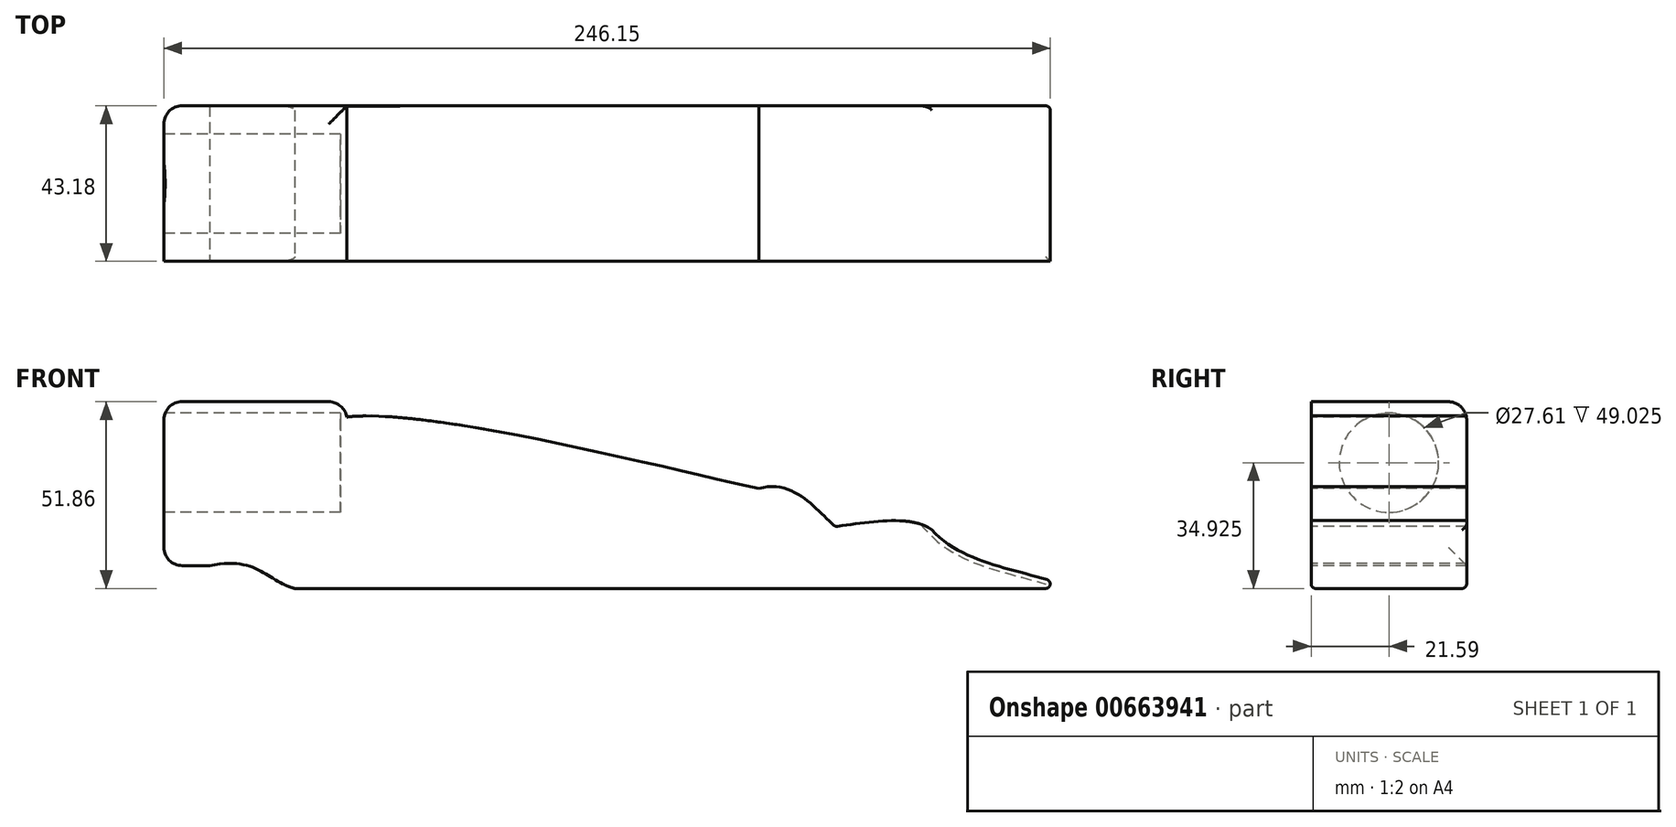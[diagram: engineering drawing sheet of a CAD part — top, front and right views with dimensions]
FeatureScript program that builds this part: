
annotation { "Feature Type Name" : "Feature", "Feature Type Description" : "" }
export const myFeature = defineFeature(function(context is Context, id is Id, definition is map)
    precondition{}
    {
        {
            var Q0;
            Q0=qCreatedBy(makeId("Front.planeOp"),FACE);
            var sketch = newSketch(context, id + "F0", { "sketchPlane" : qUnion([Q0])});
            skLineSegment(sketch, "E0", {"start": v(0, 0) * mm, "end": v(304.8, 0) * mm});
            skLineSegment(sketch, "E1", {"start": v(0, 0) * mm, "end": v(0, 69.85) * mm});
            skLineSegment(sketch, "E2", {"start": v(304.8, 0) * mm, "end": v(304.8, 17.78) * mm});
            skLineSegment(sketch, "E3", {"start": v(304.8, 17.78) * mm, "end": v(0, 69.85) * mm});
            skSolve(sketch);
        }
        {
            var Q0;
            Q0=qSketchRegion(id+"F0",true);
            extrude(context, id + "F1", {"entities" : qUnion([Q0]), "depth" : 43.18 * mm, "offsetDistance" : 25.4 * mm});
        }
        {
            var Q0;
            Q0=makeQuery(id+"F1.opExtrude","SWEPT_FACE",FACE,{"disambiguationData":[OSD([sQuery(id+"F0.wireOp",EDGE,"E1")])]});
            var sketch = newSketch(context, id + "F2", { "sketchPlane" : qUnion([Q0])});
            skCircle(sketch, "E4", {"center": v(21.59, 31.75) * mm, "radius": 9.53 * mm});
            skSolve(sketch);
        }
        {
            var Q0;
            Q0=qSketchRegion(id+"F2",true);
            extrude(context, id + "F3", {"entities" : qUnion([Q0]), "operationType" : NewBodyOperationType.REMOVE, "oppositeDirection" : true, "depth" : 53.6 * mm, "offsetDistance" : 25.4 * mm});
        }
        {
            var Q0;
            Q0=makeQuery(id+"F1.opExtrude","CAP_FACE",FACE,{"disambiguationData":[OSD([sQuery(id+"F0.wireOp",EDGE,"E0"),sQuery(id+"F0.wireOp",EDGE,"E1"),sQuery(id+"F0.wireOp",EDGE,"E2"),sQuery(id+"F0.wireOp",EDGE,"E3")])],"isStart":false});
            var sketch = newSketch(context, id + "F4", { "sketchPlane" : qUnion([Q0])});
            skLineSegment(sketch, "E5", {"start": v(304.8, 0) * mm, "end": v(266.7, 0) * mm});
            skLineSegment(sketch, "E6", {"start": v(241.3, 0) * mm, "end": v(88.9, 0) * mm});
            skLineSegment(sketch, "E7", {"start": v(88.9, 0) * mm, "end": v(63.5, 0) * mm});
            skPoint(sketch, "E8.endSnap0", {"position": v(78.27, 15.43) * mm});
            skLineSegment(sketch, "E9", {"start": v(65.27, 6.35) * mm, "end": v(52.57, 6.35) * mm});
            skLineSegment(sketch, "E10", {"start": v(52.57, 6.35) * mm, "end": v(52.57, 19.05) * mm});
            skFitSpline(sketch, "E11", {"points": [v(52.57, 19.05) * mm, v(103.37, 16.37) * mm], "startDerivative": vector(34.85, 81.56) * mm, "endDerivative": vector(14.83, -30.93) * mm});
            skLineSegment(sketch, "E12", {"start": v(103.37, 16.37) * mm, "end": v(230.37, 16.37) * mm});
            skFitSpline(sketch, "E13", {"points": [v(230.37, 16.37) * mm, v(265.73, 16.37) * mm], "startDerivative": vector(29.44, 0) * mm, "endDerivative": vector(22.85, -16.56) * mm});
            skFitSpline(sketch, "E14", {"points": [v(265.73, 16.37) * mm, v(304.8, 0) * mm], "startDerivative": vector(28.83, -31.6) * mm, "endDerivative": vector(39.07, -16.37) * mm});
            skFitSpline(sketch, "E15", {"points": [v(240.19, 16.37) * mm, v(217.83, 27.75) * mm], "startDerivative": vector(-15.82, 10.62) * mm, "endDerivative": vector(-32.32, -9.14) * mm});
            skLineSegment(sketch, "E16", {"start": v(217.83, 27.75) * mm, "end": v(70.73, 32.81) * mm});
            skLineSegment(sketch, "E17", {"start": v(103.37, 47.62) * mm, "end": v(103.37, 51.86) * mm});
            skFitSpline(sketch, "E18", {"points": [v(217.83, 27.75) * mm, v(103.37, 31.69) * mm], "startDerivative": vector(-110.48, 24.29) * mm, "endDerivative": vector(117.46, -104.1) * mm});
            skLineSegment(sketch, "E19", {"start": v(70.73, 32.81) * mm, "end": v(52.57, 32.81) * mm});
            skLineSegment(sketch, "E20", {"start": v(52.57, 32.81) * mm, "end": v(52.57, 51.86) * mm});
            skLineSegment(sketch, "E21", {"start": v(52.57, 51.86) * mm, "end": v(103.37, 51.86) * mm});
            skLineSegment(sketch, "E22", {"start": v(63.5, 0) * mm, "end": v(88.9, 0) * mm});
            skFitSpline(sketch, "E23", {"points": [v(65.27, 6.35) * mm, v(88.9, 0) * mm], "startDerivative": vector(40.25, 8.24) * mm, "endDerivative": vector(23.63, -6.35) * mm});
            skLineSegment(sketch, "E24", {"start": v(241.3, 0) * mm, "end": v(266.7, 0) * mm});
            skLineSegment(sketch, "E25", {"start": v(52.57, 32.81) * mm, "end": v(52.57, 19.05) * mm});
            skSolve(sketch);
        }
        {
            var Q0;
            {var subQ10=sQuery(id+"F4.wireOp",EDGE,"E9");Q0=makeQuery(id+"F4.imprint","IMPRINT",FACE,{"disambiguationData":[TD([[makeQuery(id+"F4.imprint","IMPRINT",EDGE,{"derivedFrom":subQ10}),1.0]])]});}
            var Q1;
            {var subQ0=sQuery(id+"F4.wireOp",EDGE,"DxxBG2hB-v0Ly-qwRo-XWPT-QvvUDP036qCp");Q1=makeQuery(id+"F4.imprint","IMPRINT",FACE,{"disambiguationData":[TD([[makeQuery(id+"F4.imprint","IMPRINT",EDGE,{"derivedFrom":subQ0}),1.0]])]});}
            var Q2;
            {var subQ0=sQuery(id+"F4.wireOp",EDGE,"E7");Q2=makeQuery(id+"F4.imprint","IMPRINT",FACE,{"disambiguationData":[TD([[makeQuery(id+"F4.imprint","IMPRINT",EDGE,{"derivedFrom":subQ0}),1.0]])]});}
            extrude(context, id + "F5", {"entities" : qUnion([Q0, Q1, Q2]), "operationType" : NewBodyOperationType.REMOVE, "oppositeDirection" : true, "depth" : 71.12 * mm, "offsetDistance" : 25.4 * mm});
        }
        {
            var Q0;
            Q0=qCreatedBy(makeId("Right.planeOp"),FACE);
            var sketch = newSketch(context, id + "F6", { "sketchPlane" : qUnion([Q0])});
            skLineSegment(sketch, "E26", {"start": v(0, 0) * mm, "end": v(0, 34.93) * mm});
            skLineSegment(sketch, "E27", {"start": v(0, 34.93) * mm, "end": v(-43.18, 34.93) * mm});
            skCircle(sketch, "E28", {"center": v(-21.59, 34.93) * mm, "radius": 13.8 * mm});
            skSolve(sketch);
        }
        {
            var Q0;
            {var subQ0=sQuery(id+"F6.wireOp",EDGE,"E28");var subQ1=sQuery(id+"F6.wireOp",EDGE,"E27");var subQ2=makeQuery(id+"F6.imprint","INTERSECT",VERTEX,{"disambiguationData":[OD(0.0)],"derivedFrom":[subQ1,subQ0]});Q0=makeQuery(id+"F6.imprint","IMPRINT",FACE,{"disambiguationData":[TD([[makeQuery(id+"F6.imprint","IMPRINT",EDGE,{"disambiguationData":[TD([[subQ2,1.0]])],"derivedFrom":subQ1}),-1.0]])]});}
            var Q1;
            {var subQ0=sQuery(id+"F6.wireOp",EDGE,"E28");var subQ1=sQuery(id+"F6.wireOp",EDGE,"E27");var subQ2=makeQuery(id+"F6.imprint","INTERSECT",VERTEX,{"disambiguationData":[OD(0.0)],"derivedFrom":[subQ1,subQ0]});Q1=makeQuery(id+"F6.imprint","IMPRINT",FACE,{"disambiguationData":[TD([[makeQuery(id+"F6.imprint","IMPRINT",EDGE,{"disambiguationData":[TD([[subQ2,1.0]])],"derivedFrom":subQ1}),1.0]])]});}
            extrude(context, id + "F7", {"entities" : qUnion([Q0, Q1]), "operationType" : NewBodyOperationType.REMOVE, "depth" : 101.6 * mm, "offsetDistance" : 25.4 * mm});
        }
        {
            var Q0;
            Q0=makeQuery(id+"F5.boolean.opBoolean","COPY",EDGE,{"derivedFrom":makeQuery(id+"F5.opExtrude","CAP_EDGE",EDGE,{"disambiguationData":[OSD([sQuery(id+"F4.wireOp",EDGE,"E21")])],"isStart":true})});
            var Q1;
            Q1=makeQuery(id+"F5.boolean.opBoolean","INTERSECT",EDGE,{"derivedFrom":[makeQuery(id+"F1.opExtrude","CAP_FACE",FACE,{"disambiguationData":[OSD([sQuery(id+"F0.wireOp",EDGE,"E0"),sQuery(id+"F0.wireOp",EDGE,"E1"),sQuery(id+"F0.wireOp",EDGE,"E2"),sQuery(id+"F0.wireOp",EDGE,"E3")])],"isStart":true}),makeQuery(id+"F5.opExtrude","SWEPT_FACE",FACE,{"disambiguationData":[OSD([sQuery(id+"F4.wireOp",EDGE,"E21")])]})]});
            var Q2;
            Q2=makeQuery(id+"F5.boolean.opBoolean","COPY",EDGE,{"derivedFrom":makeQuery(id+"F5.opExtrude","SWEPT_EDGE",EDGE,{"disambiguationData":[OSD([sQuery(id+"F4.wireOp",EDGE,"E20"),sQuery(id+"F4.wireOp",EDGE,"E21")])]})});
            var Q3;
            Q3=makeQuery(id+"F5.boolean.opBoolean","COPY",EDGE,{"derivedFrom":makeQuery(id+"F5.opExtrude","SWEPT_EDGE",EDGE,{"disambiguationData":[OSD([sQuery(id+"F4.wireOp",EDGE,"E17"),sQuery(id+"F4.wireOp",EDGE,"E21")])]})});
            fillet(context, id + "F8", {"entities" : qUnion([Q0, Q1, Q2, Q3]), "radius" : 5.08 * mm, "tangentPropagation" : true, "allowEdgeOverflow" : false});
        }
        {
            var Q0;
            {var subQ0=sQuery(id+"F4.wireOp",EDGE,"E19");var subQ1=sQuery(id+"F4.wireOp",EDGE,"E20");Q0=makeQuery(id+"F5.boolean.opBoolean","COPY",EDGE,{"disambiguationData":[TD([makeQuery(id+"F1.opExtrude","CAP_FACE",FACE,{"disambiguationData":[OSD([sQuery(id+"F0.wireOp",EDGE,"E0"),sQuery(id+"F0.wireOp",EDGE,"E1"),sQuery(id+"F0.wireOp",EDGE,"E2"),sQuery(id+"F0.wireOp",EDGE,"E3")])],"isStart":false})])],"derivedFrom":makeQuery(id+"F5.opExtrude","SWEPT_EDGE",EDGE,{"disambiguationData":[OSD([subQ0,subQ1])]})});}
            var Q1;
            {var subQ0=sQuery(id+"F4.wireOp",EDGE,"E19");var subQ1=sQuery(id+"F4.wireOp",EDGE,"E20");Q1=makeQuery(id+"F5.boolean.opBoolean","COPY",EDGE,{"disambiguationData":[TD([makeQuery(id+"F1.opExtrude","CAP_FACE",FACE,{"disambiguationData":[OSD([sQuery(id+"F0.wireOp",EDGE,"E0"),sQuery(id+"F0.wireOp",EDGE,"E1"),sQuery(id+"F0.wireOp",EDGE,"E2"),sQuery(id+"F0.wireOp",EDGE,"E3")])],"isStart":true})])],"derivedFrom":makeQuery(id+"F5.opExtrude","SWEPT_EDGE",EDGE,{"disambiguationData":[OSD([subQ0,subQ1])]})});}
            var Q2;
            Q2=makeQuery(id+"F5.boolean.opBoolean","INTERSECT",EDGE,{"derivedFrom":[makeQuery(id+"F1.opExtrude","CAP_FACE",FACE,{"disambiguationData":[OSD([sQuery(id+"F0.wireOp",EDGE,"E0"),sQuery(id+"F0.wireOp",EDGE,"E1"),sQuery(id+"F0.wireOp",EDGE,"E2"),sQuery(id+"F0.wireOp",EDGE,"E3")])],"isStart":true}),makeQuery(id+"F5.opExtrude","SWEPT_FACE",FACE,{"disambiguationData":[OSD([sQuery(id+"F4.wireOp",EDGE,"E20")])]})]});
            var Q3;
            Q3=makeQuery(id+"F5.boolean.opBoolean","COPY",EDGE,{"derivedFrom":makeQuery(id+"F5.opExtrude","CAP_EDGE",EDGE,{"disambiguationData":[OSD([sQuery(id+"F4.wireOp",EDGE,"E20")])],"isStart":true})});
            var Q4;
            Q4=makeQuery(id+"F5.boolean.opBoolean","COPY",EDGE,{"derivedFrom":makeQuery(id+"F5.opExtrude","SWEPT_EDGE",EDGE,{"disambiguationData":[OSD([sQuery(id+"F4.wireOp",EDGE,"E10"),sQuery(id+"F4.wireOp",EDGE,"E11")])]})});
            var Q5;
            Q5=makeQuery(id+"F5.boolean.opBoolean","COPY",EDGE,{"derivedFrom":makeQuery(id+"F5.opExtrude","SWEPT_EDGE",EDGE,{"disambiguationData":[OSD([sQuery(id+"F4.wireOp",EDGE,"E9"),sQuery(id+"F4.wireOp",EDGE,"E10")])]})});
            fillet(context, id + "F9", {"entities" : qUnion([Q0, Q1, Q2, Q3, Q4, Q5]), "radius" : 5.08 * mm, "tangentPropagation" : true, "allowEdgeOverflow" : false});
        }
        {
            var Q0;
            Q0=makeQuery(id+"F5.boolean.opBoolean","COPY",EDGE,{"derivedFrom":makeQuery(id+"F5.opExtrude","SWEPT_EDGE",EDGE,{"disambiguationData":[OSD([sQuery(id+"F4.wireOp",EDGE,"E13"),sQuery(id+"F4.wireOp",EDGE,"E14")])]})});
            var Q1;
            Q1=makeQuery(id+"F5.boolean.opBoolean","COPY",EDGE,{"derivedFrom":makeQuery(id+"F5.opExtrude","SWEPT_EDGE",EDGE,{"disambiguationData":[OSD([sQuery(id+"F4.wireOp",EDGE,"E13"),sQuery(id+"F4.wireOp",EDGE,"E15")])]})});
            var Q2;
            {var subQ0=sQuery(id+"F0.wireOp",EDGE,"E2");Q2=makeQuery(id+"F5.boolean.opBoolean","MERGE",EDGE,{"derivedFrom":[makeQuery(id+"F1.opExtrude","SWEPT_EDGE",EDGE,{"disambiguationData":[OSD([sQuery(id+"F0.wireOp",EDGE,"E0"),subQ0])]}),makeQuery(id+"F5.opExtrude","SWEPT_EDGE",EDGE,{"disambiguationData":[OSD([subQ0,sQuery(id+"F4.wireOp",EDGE,"E5"),sQuery(id+"F4.wireOp",EDGE,"E14")])]})]});}
            var Q3;
            {var subQ0=sQuery(id+"F0.wireOp",EDGE,"E0");Q3=makeQuery(id+"F5.boolean.opBoolean","SPLIT",EDGE,{"disambiguationData":[TD([makeQuery(id+"F5.opExtrude","SWEPT_FACE",FACE,{"disambiguationData":[OSD([sQuery(id+"F4.wireOp",EDGE,"E14")])]})])],"derivedFrom":makeQuery(id+"F1.opExtrude","CAP_EDGE",EDGE,{"disambiguationData":[OSD([subQ0])],"isStart":false})});}
            var Q4;
            {var subQ0=sQuery(id+"F0.wireOp",EDGE,"E0");Q4=makeQuery(id+"F5.boolean.opBoolean","SPLIT",EDGE,{"disambiguationData":[TD([makeQuery(id+"F5.opExtrude","SWEPT_FACE",FACE,{"disambiguationData":[OSD([sQuery(id+"F4.wireOp",EDGE,"E14")])]})])],"derivedFrom":makeQuery(id+"F1.opExtrude","CAP_EDGE",EDGE,{"disambiguationData":[OSD([subQ0])],"isStart":true})});}
            var Q5;
            Q5=makeQuery(id+"F5.boolean.opBoolean","INTERSECT",EDGE,{"derivedFrom":[makeQuery(id+"F1.opExtrude","CAP_FACE",FACE,{"disambiguationData":[OSD([sQuery(id+"F0.wireOp",EDGE,"E0"),sQuery(id+"F0.wireOp",EDGE,"E1"),sQuery(id+"F0.wireOp",EDGE,"E2"),sQuery(id+"F0.wireOp",EDGE,"E3")])],"isStart":true}),makeQuery(id+"F5.opExtrude","SWEPT_FACE",FACE,{"disambiguationData":[OSD([sQuery(id+"F4.wireOp",EDGE,"E14")])]})]});
            var Q6;
            Q6=makeQuery(id+"F5.boolean.opBoolean","COPY",EDGE,{"derivedFrom":makeQuery(id+"F5.opExtrude","CAP_EDGE",EDGE,{"disambiguationData":[OSD([sQuery(id+"F4.wireOp",EDGE,"E14")])],"isStart":true})});
            fillet(context, id + "F10", {"entities" : qUnion([Q0, Q1, Q2, Q3, Q4, Q5, Q6]), "radius" : 1.25 * mm, "tangentPropagation" : true, "allowEdgeOverflow" : false});
        }
    });
